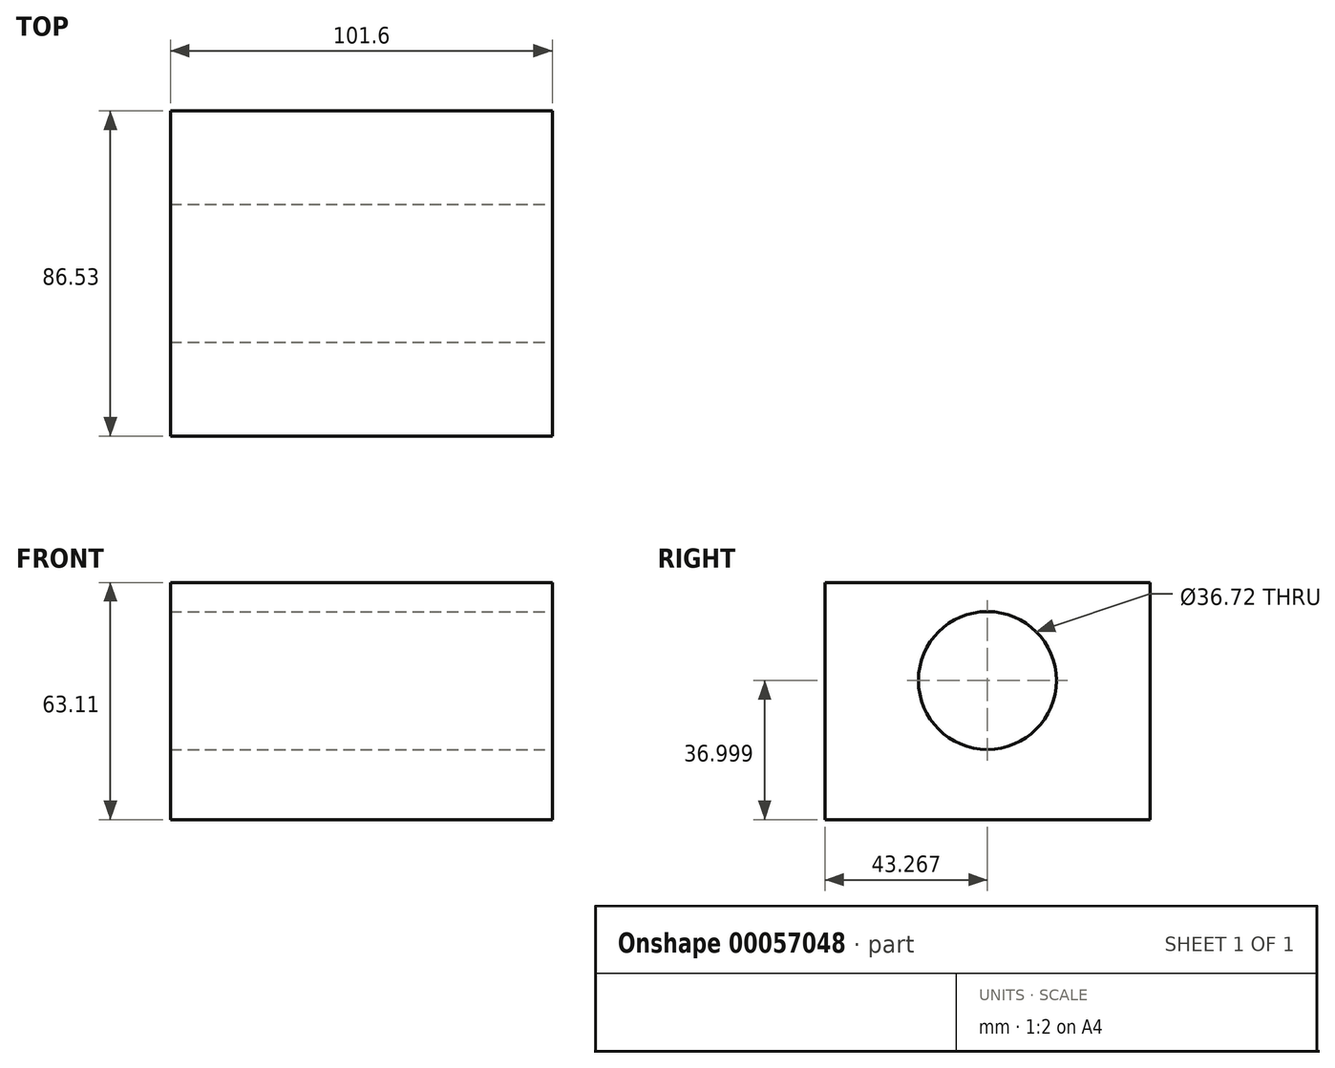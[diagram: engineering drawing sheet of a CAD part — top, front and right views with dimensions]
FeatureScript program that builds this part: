
annotation { "Feature Type Name" : "Feature", "Feature Type Description" : "" }
export const myFeature = defineFeature(function(context is Context, id is Id, definition is map)
    precondition{}
    {
        {
            var Q0;
            Q0=qCreatedBy(makeId("Right.planeOp"),FACE);
            var sketch = newSketch(context, id + "F0", { "sketchPlane" : qUnion([Q0])});
            skLineSegment(sketch, "E0.bottom", {"start": v(-49.65, 63.1) * mm, "end": v(36.88, 63.1) * mm});
            skLineSegment(sketch, "E0.top", {"start": v(-49.65, 0) * mm, "end": v(36.88, 0) * mm});
            skLineSegment(sketch, "E0.left", {"start": v(-49.65, 63.1) * mm, "end": v(-49.65, 0) * mm});
            skLineSegment(sketch, "E0.right", {"start": v(36.88, 63.1) * mm, "end": v(36.88, 0) * mm});
            skSolve(sketch);
        }
        {
            var Q0;
            Q0=makeQuery(id+"F0.imprint","IMPRINT",FACE,{"disambiguationData":[TD([[makeQuery(id+"F0.imprint","IMPRINT",EDGE,{"derivedFrom":sQuery(id+"F0.wireOp",EDGE,"E0.bottom")}),-1.0]])]});
            extrude(context, id + "F1", {"entities" : qUnion([Q0]), "depth" : 101.6 * mm});
        }
        {
            var Q0;
            Q0=makeQuery(id+"F1.opExtrude","CAP_FACE",FACE,{"disambiguationData":[OSD([sQuery(id+"F0.wireOp",EDGE,"E0.bottom"),sQuery(id+"F0.wireOp",EDGE,"E0.top"),sQuery(id+"F0.wireOp",EDGE,"E0.left"),sQuery(id+"F0.wireOp",EDGE,"E0.right")])],"isStart":false});
            var sketch = newSketch(context, id + "F2", { "sketchPlane" : qUnion([Q0])});
            skCircle(sketch, "E1", {"center": v(-6.38, 37) * mm, "radius": 18.36 * mm});
            skPoint(sketch, "E1.centerSnap0", {"position": v(-6.38, 0) * mm});
            skSolve(sketch);
        }
        {
            var Q0;
            Q0=makeQuery(id+"F2.imprint","IMPRINT",FACE,{"disambiguationData":[TD([[makeQuery(id+"F2.imprint","IMPRINT",EDGE,{"derivedFrom":sQuery(id+"F2.wireOp",EDGE,"E1")}),1.0]])]});
            extrude(context, id + "F3", {"entities" : qUnion([Q0]), "operationType" : NewBodyOperationType.REMOVE, "endBound" : BoundingType.THROUGH_ALL, "oppositeDirection" : true, "depth" : 25.4 * mm});
        }
    });
